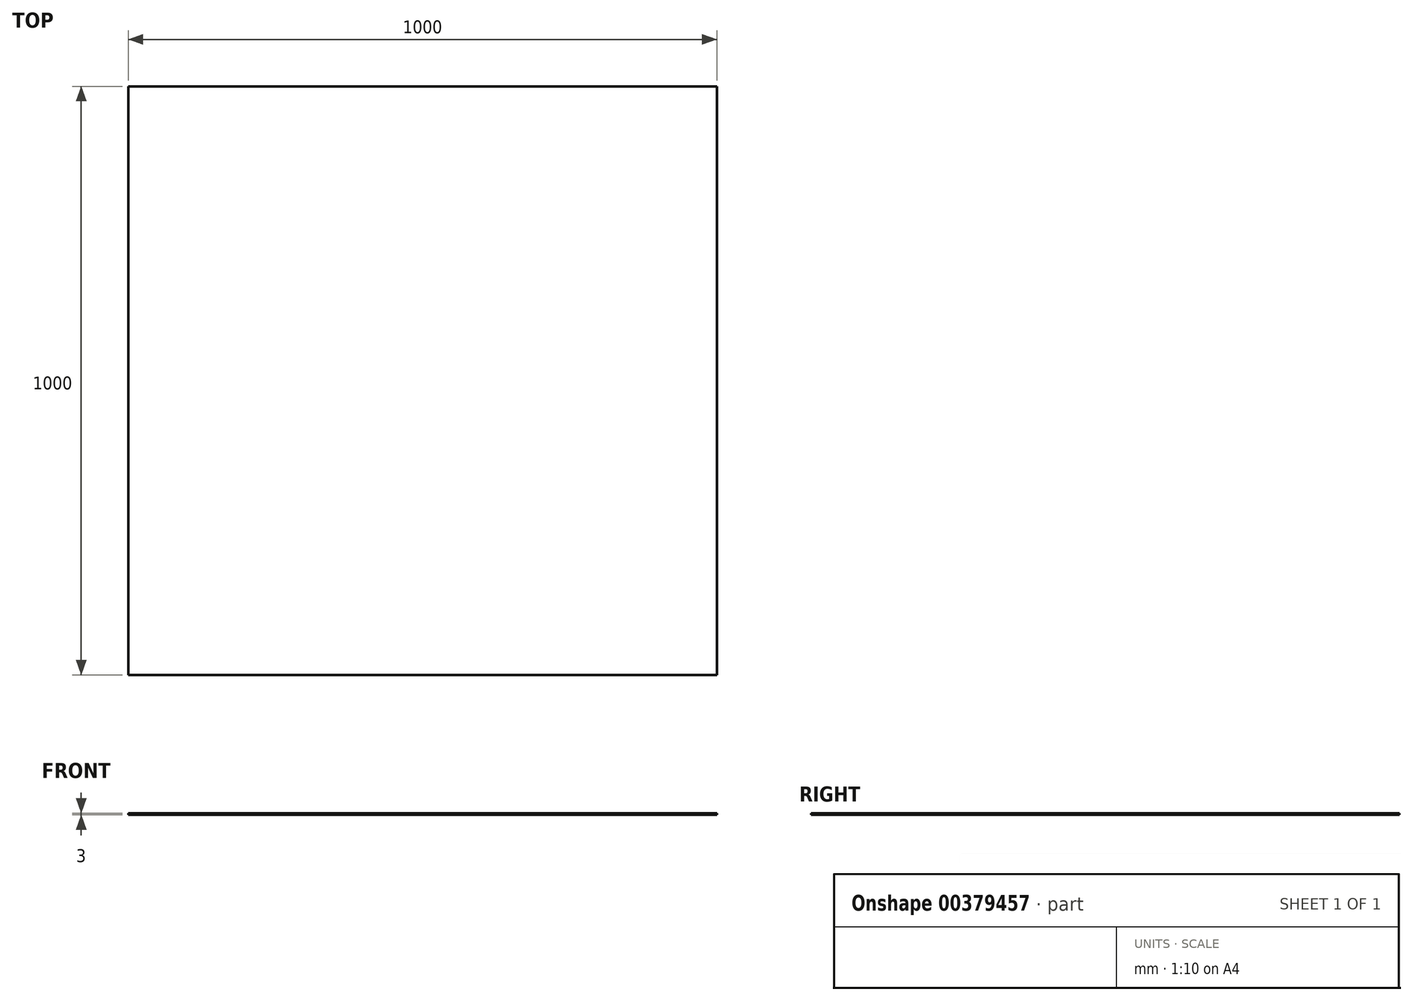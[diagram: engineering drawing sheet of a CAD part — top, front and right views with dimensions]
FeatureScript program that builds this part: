
annotation { "Feature Type Name" : "Feature", "Feature Type Description" : "" }
export const myFeature = defineFeature(function(context is Context, id is Id, definition is map)
    precondition{}
    {
        {
            var Q0;
            Q0=qCreatedBy(makeId("Top.planeOp"),FACE);
            var sketch = newSketch(context, id + "F0", { "sketchPlane" : qUnion([Q0])});
            skLineSegment(sketch, "E0.bottom", {"start": v(-500, 500) * mm, "end": v(500, 500) * mm});
            skLineSegment(sketch, "E0.top", {"start": v(-500, -500) * mm, "end": v(500, -500) * mm});
            skLineSegment(sketch, "E0.left", {"start": v(-500, 500) * mm, "end": v(-500, -500) * mm});
            skLineSegment(sketch, "E0.right", {"start": v(500, 500) * mm, "end": v(500, -500) * mm});
            skPoint(sketch, "E0.middle", {"position": v(0, 0) * mm});
            skSolve(sketch);
        }
        {
            var Q0;
            Q0=makeQuery(id+"F0.imprint","IMPRINT",FACE,{"disambiguationData":[TD([[makeQuery(id+"F0.imprint","IMPRINT",EDGE,{"derivedFrom":sQuery(id+"F0.wireOp",EDGE,"E0.bottom")}),-1.0]])]});
            extrude(context, id + "F1", {"entities" : qUnion([Q0]), "depth" : 3 * mm});
        }
    });
